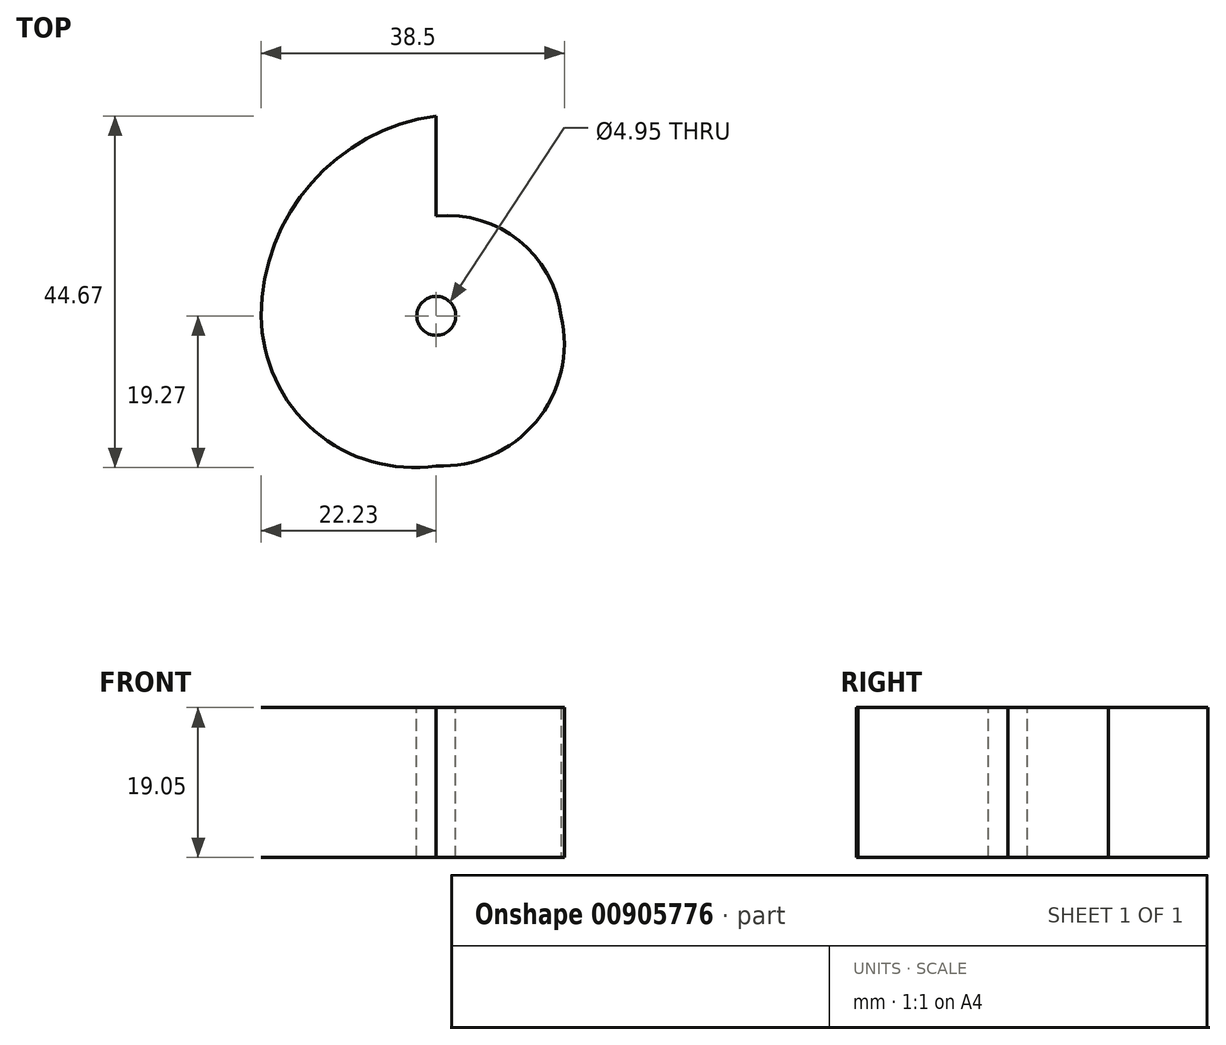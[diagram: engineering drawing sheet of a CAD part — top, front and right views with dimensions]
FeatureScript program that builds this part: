
annotation { "Feature Type Name" : "Feature", "Feature Type Description" : "" }
export const myFeature = defineFeature(function(context is Context, id is Id, definition is map)
    precondition{}
    {
        {
            var Q0;
            Q0=qCreatedBy(makeId("Top.planeOp"),FACE);
            var sketch = newSketch(context, id + "F0", { "sketchPlane" : qUnion([Q0])});
            skLineSegment(sketch, "E0", {"start": v(0, 0) * mm, "end": v(0, 25.4) * mm});
            skLineSegment(sketch, "E1", {"start": v(0, 0) * mm, "end": v(0, 12.7) * mm});
            skLineSegment(sketch, "E2", {"start": v(0, 0) * mm, "end": v(0, -19.05) * mm});
            skLineSegment(sketch, "E3", {"start": v(0, 0) * mm, "end": v(-22.23, 0) * mm});
            skLineSegment(sketch, "E4", {"start": v(0, 0) * mm, "end": v(15.88, 0) * mm});
            skArc(sketch, "E5", {"start": v(0, 25.4) * mm, "mid": v(-15.87, 16.86) * mm, "end": v(-22.22, 0) * mm});
            skArc(sketch, "E6", {"start": v(-22.23, 0) * mm, "mid": v(-15.47, -14.61) * mm, "end": v(0, -19.05) * mm});
            skArc(sketch, "E7", {"start": v(0, -19.05) * mm, "mid": v(12.66, -13.46) * mm, "end": v(15.88, 0) * mm});
            skArc(sketch, "E8", {"start": v(15.88, 0) * mm, "mid": v(10.5, 9.56) * mm, "end": v(0, 12.7) * mm});
            skSolve(sketch);
        }
        {
            var Q0;
            Q0=makeQuery(id+"F0.imprint","IMPRINT",FACE,{"disambiguationData":[TD([[makeQuery(id+"F0.imprint","IMPRINT",EDGE,{"derivedFrom":sQuery(id+"F0.wireOp",EDGE,"E2")}),-1.0]])]});
            var Q1;
            {var subQ0=sQuery(id+"F0.wireOp",EDGE,"E3");Q1=makeQuery(id+"F0.imprint","IMPRINT",FACE,{"disambiguationData":[TD([[makeQuery(id+"F0.imprint","IMPRINT",EDGE,{"derivedFrom":subQ0}),-1.0]])]});}
            var Q2;
            Q2=makeQuery(id+"F0.imprint","IMPRINT",FACE,{"disambiguationData":[TD([[makeQuery(id+"F0.imprint","IMPRINT",EDGE,{"derivedFrom":sQuery(id+"F0.wireOp",EDGE,"E2")}),1.0]])]});
            var Q3;
            {var subQ0=sQuery(id+"F0.wireOp",EDGE,"E4");Q3=makeQuery(id+"F0.imprint","IMPRINT",FACE,{"disambiguationData":[TD([[makeQuery(id+"F0.imprint","IMPRINT",EDGE,{"derivedFrom":subQ0}),1.0]])]});}
            extrude(context, id + "F1", {"entities" : qUnion([Q0, Q1, Q2, Q3]), "depth" : 19.05 * mm, "offsetDistance" : 25.4 * mm});
        }
        {
            var Q0;
            Q0=makeQuery(id+"F1.opExtrude","CAP_FACE",FACE,{"disambiguationData":[OSD([sQuery(id+"F0.wireOp",EDGE,"E0"),sQuery(id+"F0.wireOp",EDGE,"E5"),sQuery(id+"F0.wireOp",EDGE,"E6"),sQuery(id+"F0.wireOp",EDGE,"E7"),sQuery(id+"F0.wireOp",EDGE,"E8")])],"isStart":false});
            var sketch = newSketch(context, id + "F2", { "sketchPlane" : qUnion([Q0])});
            skCircle(sketch, "E9", {"center": v(0, 0) * mm, "radius": 2.48 * mm});
            skSolve(sketch);
        }
        {
            var Q0;
            Q0=makeQuery(id+"F2.imprint","IMPRINT",FACE,{"disambiguationData":[TD([[makeQuery(id+"F2.imprint","IMPRINT",EDGE,{"derivedFrom":sQuery(id+"F2.wireOp",EDGE,"E9")}),1.0]])]});
            extrude(context, id + "F3", {"entities" : qUnion([Q0]), "operationType" : NewBodyOperationType.REMOVE, "oppositeDirection" : true, "depth" : 25.4 * mm, "offsetDistance" : 25.4 * mm});
        }
    });
